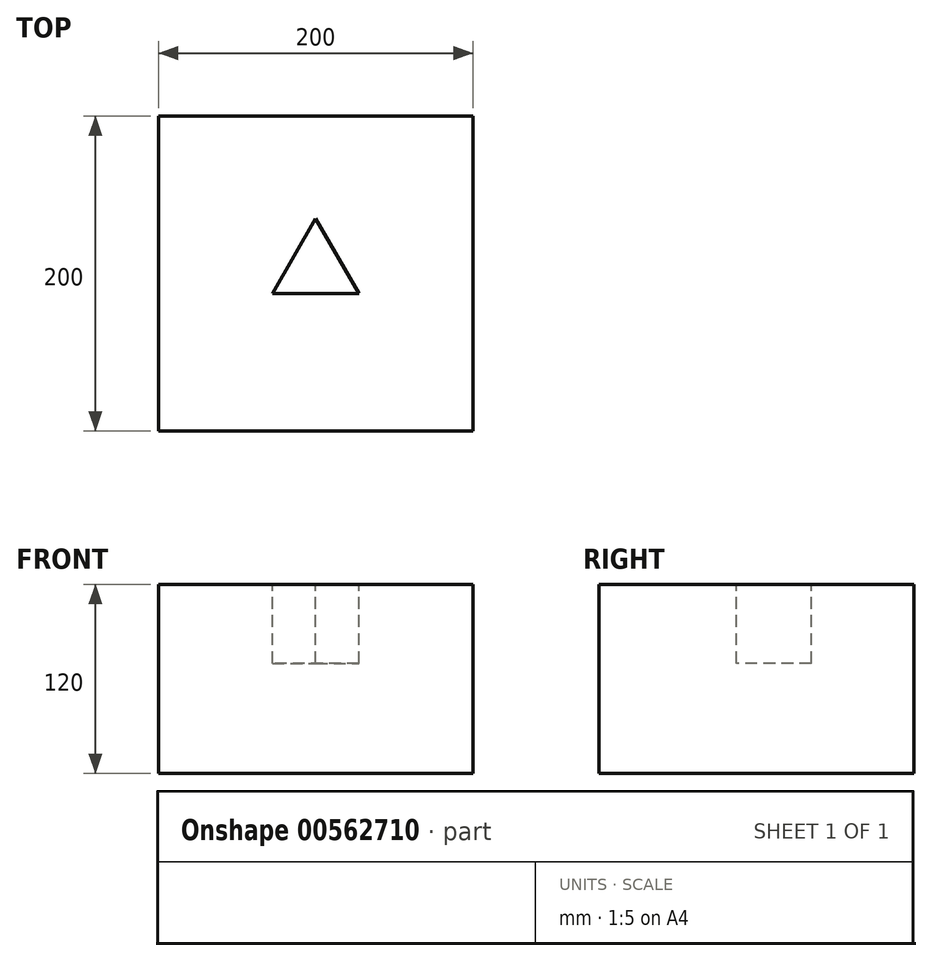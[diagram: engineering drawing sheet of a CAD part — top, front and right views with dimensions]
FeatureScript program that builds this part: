
annotation { "Feature Type Name" : "Feature", "Feature Type Description" : "" }
export const myFeature = defineFeature(function(context is Context, id is Id, definition is map)
    precondition{}
    {
        {
            var Q0;
            Q0=qCreatedBy(makeId("Top.planeOp"),FACE);
            var sketch = newSketch(context, id + "F0", { "sketchPlane" : qUnion([Q0])});
            skLineSegment(sketch, "E0.bottom", {"start": v(100, 100) * mm, "end": v(-100, 100) * mm});
            skLineSegment(sketch, "E0.top", {"start": v(100, -100) * mm, "end": v(-100, -100) * mm});
            skLineSegment(sketch, "E0.left", {"start": v(100, 100) * mm, "end": v(100, -100) * mm});
            skLineSegment(sketch, "E0.right", {"start": v(-100, 100) * mm, "end": v(-100, -100) * mm});
            skPoint(sketch, "E0.middle", {"position": v(0, 0) * mm});
            skSolve(sketch);
        }
        {
            var Q0;
            Q0 = qSketchRegion(id + "F0", true);
            extrude(context, id + "F1", {"entities" : qUnion([Q0]), "depth" : 120 * mm, "offsetDistance" : 25.4 * mm});
        }
        {
            var Q0;
            Q0=makeQuery(id+"F1.opExtrude","CAP_FACE",FACE,{"disambiguationData":[OSD([sQuery(id+"F0.wireOp",EDGE,"E0.bottom"),sQuery(id+"F0.wireOp",EDGE,"E0.top"),sQuery(id+"F0.wireOp",EDGE,"E0.left"),sQuery(id+"F0.wireOp",EDGE,"E0.right")])],"isStart":false});
            var sketch = newSketch(context, id + "F2", { "sketchPlane" : qUnion([Q0])});
            skLineSegment(sketch, "E1.0", {"start": v(27.5, -12.82) * mm, "end": v(-27.5, -12.82) * mm});
            skLineSegment(sketch, "E1.1", {"start": v(-27.5, -12.82) * mm, "end": v(0, 34.81) * mm});
            skLineSegment(sketch, "E1.2", {"start": v(0, 34.81) * mm, "end": v(27.5, -12.82) * mm});
            skSolve(sketch);
        }
        {
            var Q0;
            Q0=makeQuery(id+"F2.imprint","IMPRINT",FACE,{"disambiguationData":[TD([[makeQuery(id+"F2.imprint","IMPRINT",EDGE,{"derivedFrom":sQuery(id+"F2.wireOp",EDGE,"E1.0")}),-1.0]])]});
            extrude(context, id + "F3", {"entities" : qUnion([Q0]), "operationType" : NewBodyOperationType.REMOVE, "oppositeDirection" : true, "depth" : 50 * mm, "offsetDistance" : 25.4 * mm});
        }
    });
